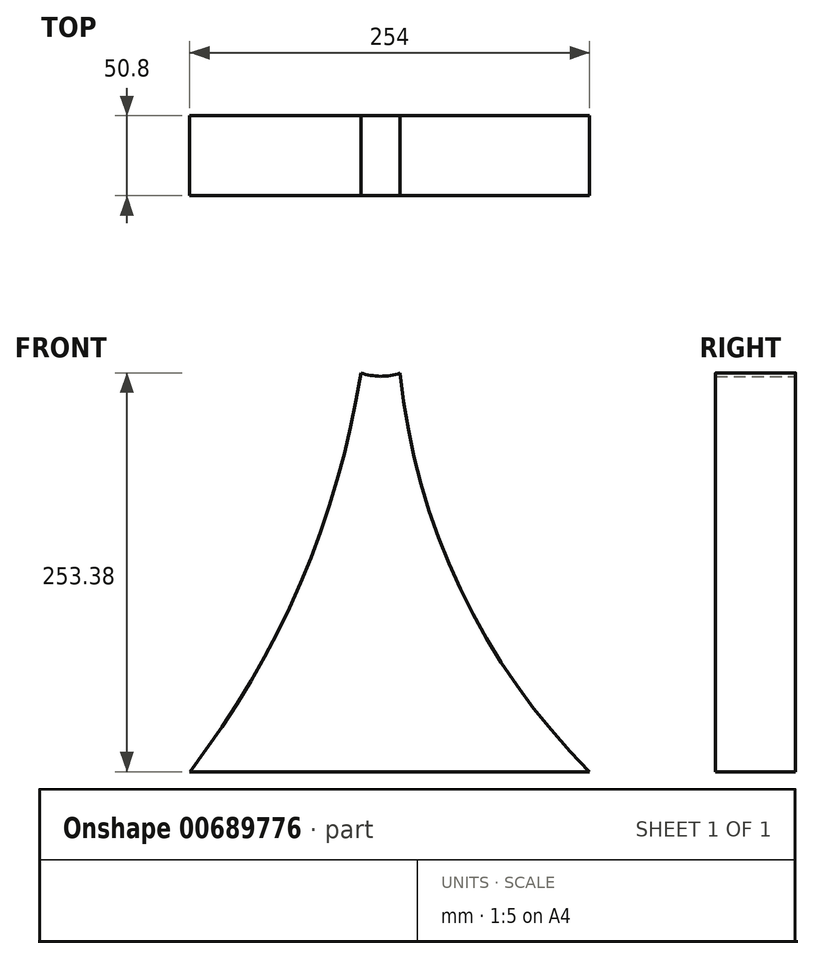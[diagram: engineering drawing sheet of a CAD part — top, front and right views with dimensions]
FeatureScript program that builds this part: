
annotation { "Feature Type Name" : "Feature", "Feature Type Description" : "" }
export const myFeature = defineFeature(function(context is Context, id is Id, definition is map)
    precondition{}
    {
        {
            var Q0;
            Q0=qCreatedBy(makeId("Front.planeOp"),FACE);
            var sketch = newSketch(context, id + "F0", { "sketchPlane" : qUnion([Q0])});
            skLineSegment(sketch, "E0", {"start": v(-127, -127) * mm, "end": v(127, -127) * mm});
            skArc(sketch, "E1", {"start": v(-127, -127) * mm, "mid": v(-56.7, -7.16) * mm, "end": v(-18.35, 126.38) * mm});
            skArc(sketch, "E2", {"start": v(6.65, 126.12) * mm, "mid": v(44.8, -10.9) * mm, "end": v(127, -127) * mm});
            skArc(sketch, "E3", {"start": v(-18.35, 126.38) * mm, "mid": v(-5.87, 124.2) * mm, "end": v(6.65, 126.12) * mm});
            skSolve(sketch);
        }
        {
            var Q0;
            Q0 = qSketchRegion(id + "F0", true);
            var Q1;
            Q1=makeQuery(id+"F0.imprint","IMPRINT",FACE,{"disambiguationData":[TD([[makeQuery(id+"F0.imprint","IMPRINT",EDGE,{"derivedFrom":sQuery(id+"F0.wireOp",EDGE,"fXQZ3OjH-8kh1-Z59F-wT3O-D8DHyHG2iFH8")}),1.0]])]});
            extrude(context, id + "F1", {"entities" : qUnion([Q0, Q1]), "depth" : 25.4 * mm, "offsetDistance" : 25.4 * mm});
        }
        {
            var Q0;
            Q0 = qSketchRegion(id + "F0", true);
            var Q1;
            Q1=makeQuery(id+"F1.opExtrude","CAP_FACE",FACE,{"disambiguationData":[OSD([sQuery(id+"F0.wireOp",EDGE,"E0"),sQuery(id+"F0.wireOp",EDGE,"E1"),sQuery(id+"F0.wireOp",EDGE,"E2"),sQuery(id+"F0.wireOp",EDGE,"E3")])],"isStart":false});
            extrude(context, id + "F2", {"entities" : qUnion([Q0, Q1]), "operationType" : NewBodyOperationType.ADD, "oppositeDirection" : true, "depth" : 25.4 * mm, "offsetDistance" : 25.4 * mm});
        }
    });
